# Revit family: MULBA4110
name_source: partatom
category: Generic Models
revit_build: Autodesk Revit 2018 (Build: 22.0.11200.0000)
units: mm (PartAtom-declared; Revit-internal decimal feet)

## family parameters
Always vertical = Yes
Can host rebar = No
Cut with Voids When Loaded = No
OmniClass Number = 23.60.30.14
OmniClass Title = Ducting and Wireways for General Use
Part Type = Normal
Room Calculation Point = No
Round Connector Dimension = Use Diameter
Shared = No
Work Plane-Based = No

## types (1)
- Standard
    Connector_1_Diameter = 0 mm  [stored 0 ft]
    Connector_2_Diameter = 0 mm  [stored 0 ft]
    Connector_3_Diameter = 0 mm  [stored 0 ft]
    Connector_4_Diameter = 0 mm  [stored 0 ft]
    Description = Multiiduct (Tube) Adapter
    Design Status = 1
    Manufacturer = PowerCast
    Model = MULBA4110
    Part Number = MULAM26260204W110
    URL = https://trekput.nl

note: [stored X ft] marks values corroborated as IEEE doubles in the binary element streams (Revit-internal decimal feet)

## geometry (parser evidence)
native form markers: Sweep x2
no freeform markers — native parametric forms only
